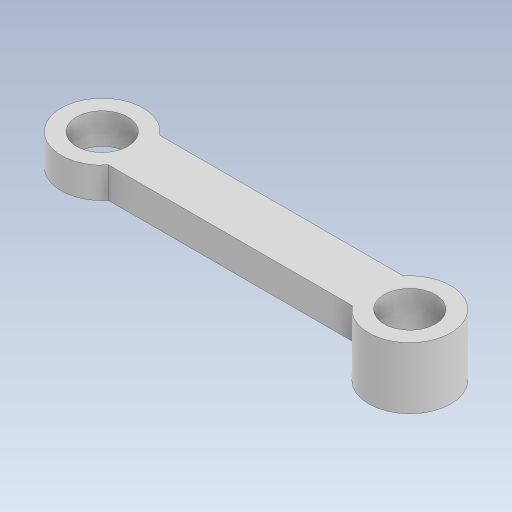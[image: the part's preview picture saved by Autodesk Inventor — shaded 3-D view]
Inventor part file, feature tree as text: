
AUTODESK INVENTOR PART (.ipt)
format: ipt  version: 2023.5 (Build 275446000, 446)  size: 276,480 bytes
history: native  units: mm
features: extrude x2, sketch x1
ambient origin geometry x8: Origin, YZ Plane, XZ Plane, XY Plane, X Axis, Y Axis, Z Axis, Center Point
bodies: Solid1 (feature_tree)
feature tree (3):
  sketch  "Sketch1"  dims[d0=5.0mm d1=8.0mm d2=5.0mm d3=8.0mm d4=30.0mm d5=3.0mm d6=0.0mm d7=3.0mm d8=0.0mm]
  extrude  "Extrusion1"  Depth=3.0mm
  extrude  "Extrusion2"  Depth=5.0mm
